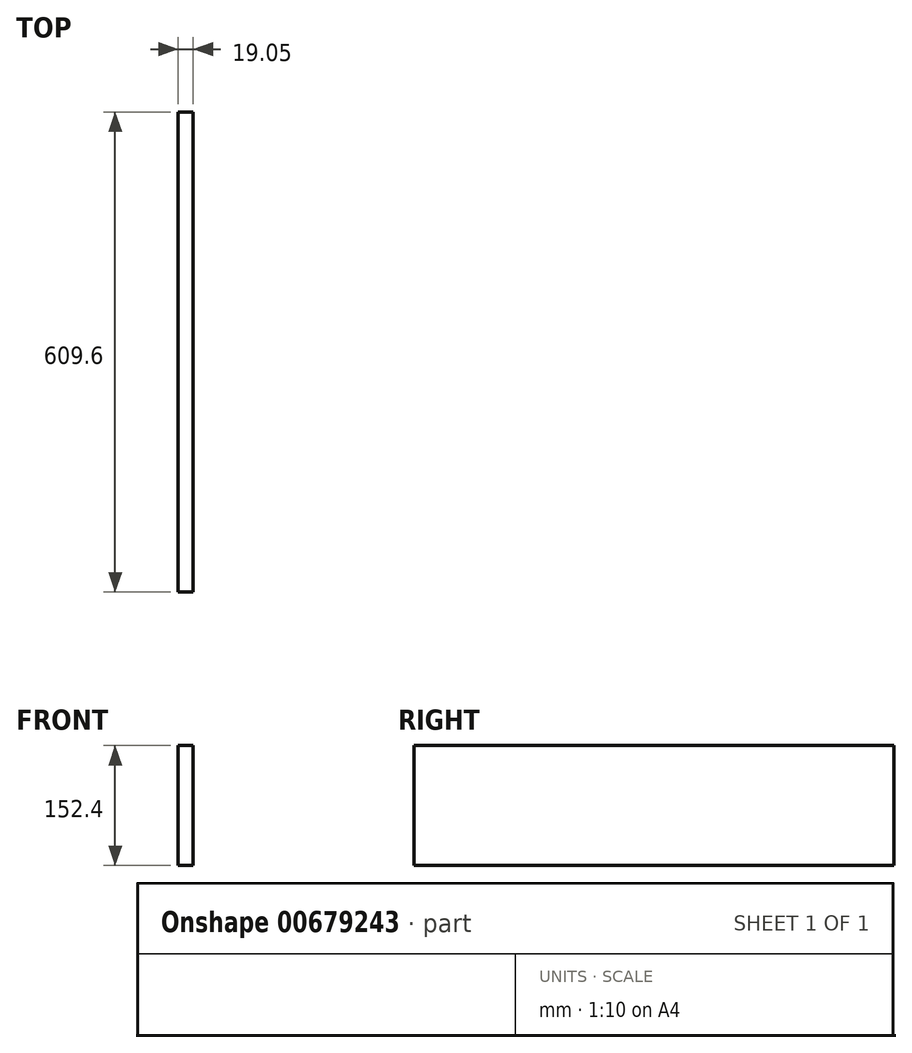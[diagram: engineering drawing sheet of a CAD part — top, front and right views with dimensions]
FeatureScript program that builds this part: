
annotation { "Feature Type Name" : "Feature", "Feature Type Description" : "" }
export const myFeature = defineFeature(function(context is Context, id is Id, definition is map)
    precondition{}
    {
        {
            var Q0;
            Q0=qCreatedBy(makeId("Right.planeOp"),FACE);
            var sketch = newSketch(context, id + "F0", { "sketchPlane" : qUnion([Q0])});
            skLineSegment(sketch, "E0.bottom", {"start": v(304.8, 76.2) * mm, "end": v(-304.8, 76.2) * mm});
            skLineSegment(sketch, "E0.top", {"start": v(304.8, -76.2) * mm, "end": v(-304.8, -76.2) * mm});
            skLineSegment(sketch, "E0.left", {"start": v(304.8, 76.2) * mm, "end": v(304.8, -76.2) * mm});
            skLineSegment(sketch, "E0.right", {"start": v(-304.8, 76.2) * mm, "end": v(-304.8, -76.2) * mm});
            skPoint(sketch, "E0.middle", {"position": v(0, 0) * mm});
            skSolve(sketch);
        }
        {
            var Q0;
            Q0=makeQuery(id+"F0.imprint","IMPRINT",FACE,{"disambiguationData":[TD([[makeQuery(id+"F0.imprint","IMPRINT",EDGE,{"derivedFrom":sQuery(id+"F0.wireOp",EDGE,"E0.bottom")}),1.0]])]});
            extrude(context, id + "F1", {"entities" : qUnion([Q0]), "depth" : 19.05 * mm, "offsetDistance" : 25.4 * mm});
        }
    });
